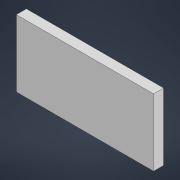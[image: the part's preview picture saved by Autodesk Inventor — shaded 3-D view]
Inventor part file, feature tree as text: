
AUTODESK INVENTOR PART (.ipt)
format: ipt  version: 2022 (Build 260153000, 153)  size: 82,944 bytes
history: native  units: mm
features: other x1, extrude x1, sketch x1
ambient origin geometry x8: Origin, YZ Plane, XZ Plane, XY Plane, X Axis, Y Axis, Z Axis, Center Point
bodies: Body1 (feature_tree)
feature tree (3):
  other  "Твердое тело1"
  extrude  "Выдавливание1"  Depth=246.0mm
  sketch  "Эскиз1"
